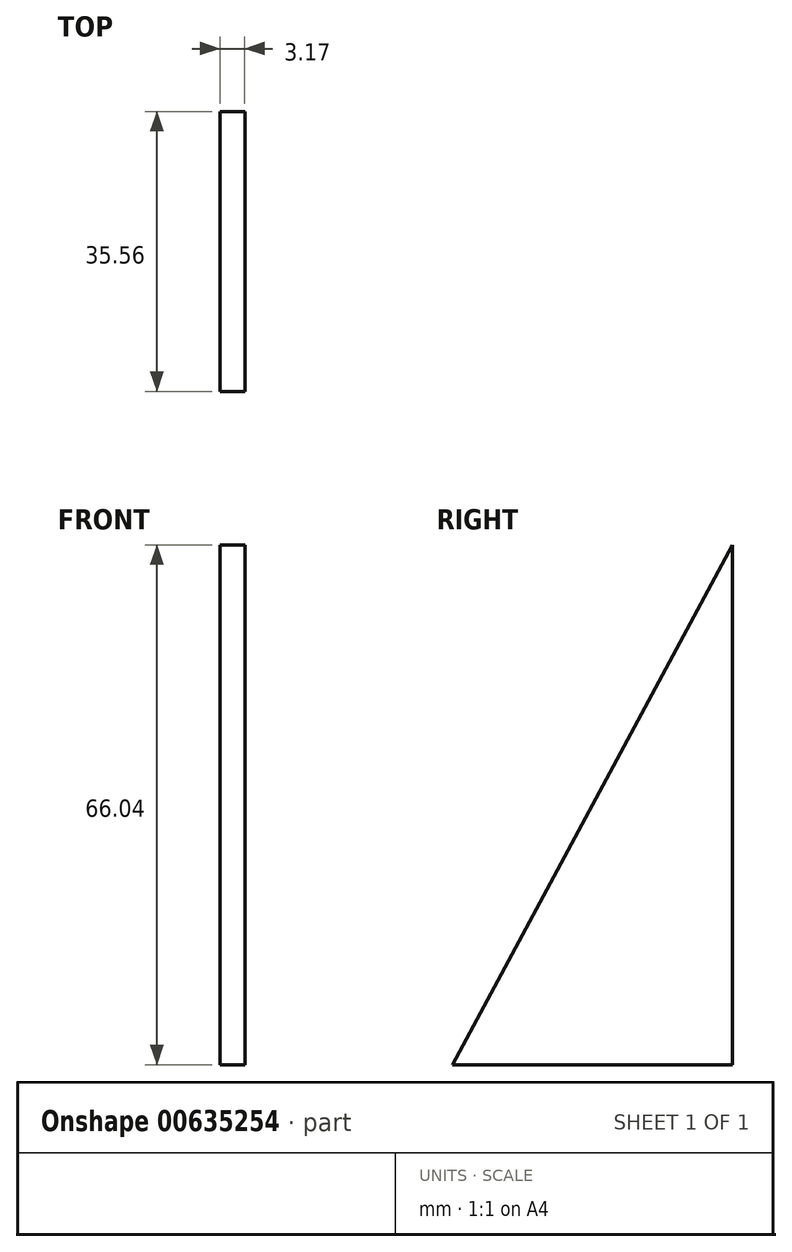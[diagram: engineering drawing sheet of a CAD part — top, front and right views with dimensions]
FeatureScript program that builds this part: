
annotation { "Feature Type Name" : "Feature", "Feature Type Description" : "" }
export const myFeature = defineFeature(function(context is Context, id is Id, definition is map)
    precondition{}
    {
        {
            var Q0;
            Q0=qCreatedBy(makeId("Right.planeOp"),FACE);
            var sketch = newSketch(context, id + "F0", { "sketchPlane" : qUnion([Q0])});
            skLineSegment(sketch, "E0", {"start": v(0, 0) * mm, "end": v(0, 66.04) * mm});
            skLineSegment(sketch, "E1", {"start": v(0, 66.04) * mm, "end": v(-35.56, 0) * mm});
            skLineSegment(sketch, "E2", {"start": v(-35.56, 0) * mm, "end": v(0, 0) * mm});
            skSolve(sketch);
        }
        {
            var Q0;
            Q0 = qSketchRegion(id + "F0", true);
            extrude(context, id + "F1", {"entities" : qUnion([Q0]), "depth" : 3.17 * mm, "offsetDistance" : 25.4 * mm});
        }
    });
